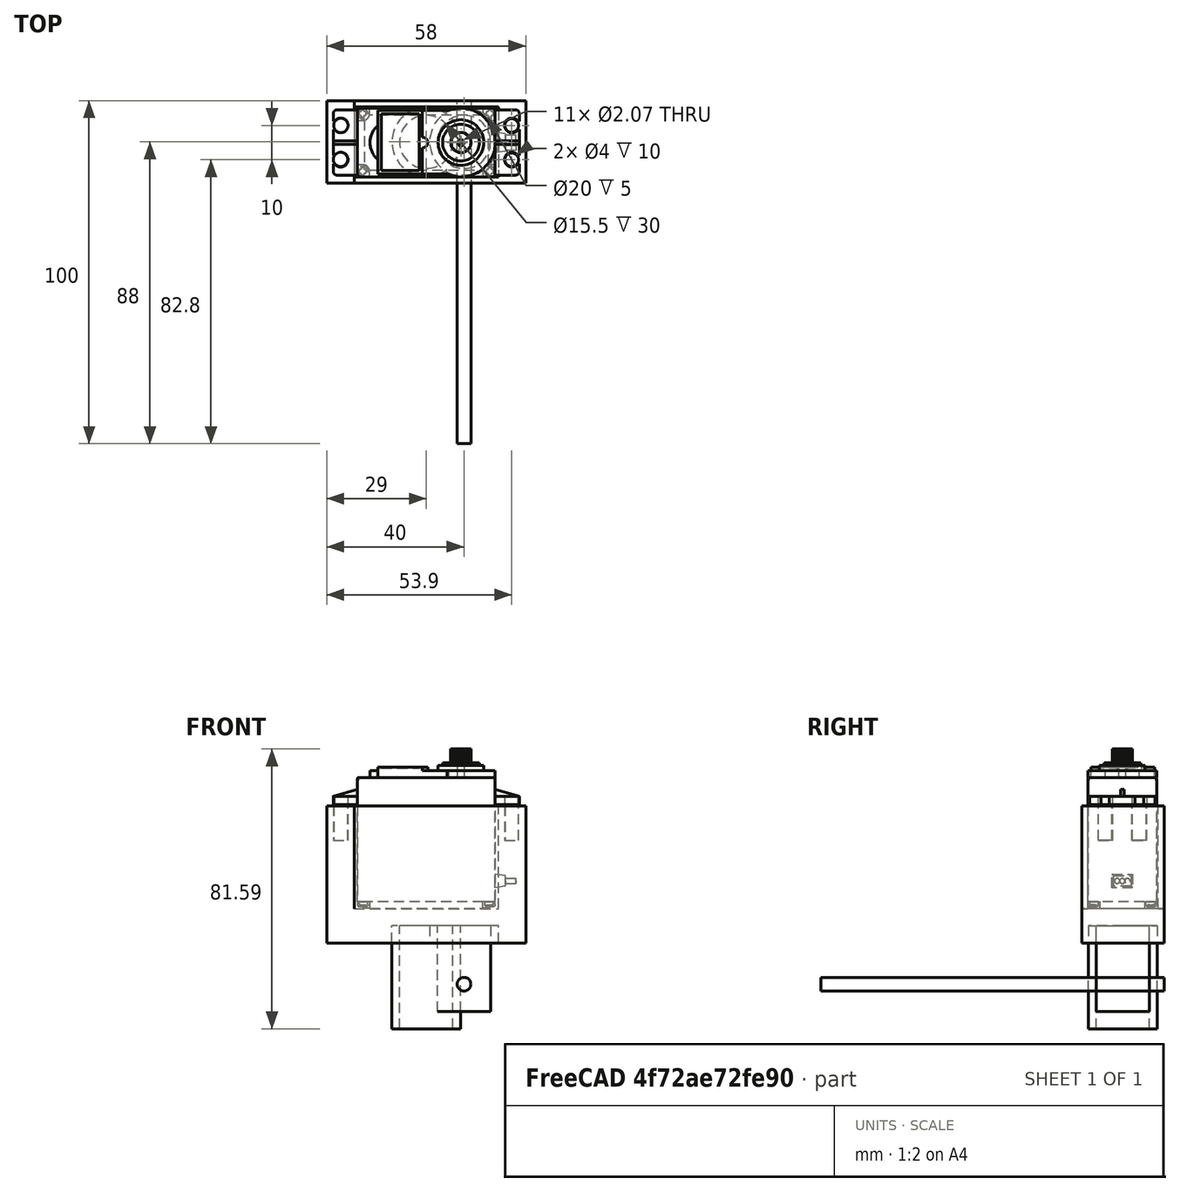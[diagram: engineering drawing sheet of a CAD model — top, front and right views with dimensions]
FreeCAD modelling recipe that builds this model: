
FCSTD DOCUMENT  (FreeCAD 0.21R33771 (Git))
Label: U_Servo_v1
License: All rights reserved
LicenseURL: http://en.wikipedia.org/wiki/All_rights_reserved
objects: Sketcher::SketchObject×5, PartDesign::Pad×3, Mesh::Feature×2, PartDesign::Pocket×2, Part::FeaturePython×1, Part::Feature×1, PartDesign::Body×1, Part::Cylinder×1
note: 19 computed .brp shape members not serialized (recipe doc carries the construction recipe); baked Part::Feature solids carry a one-line shape summary decoded from their .brp

FEATURE [Part::FeaturePython] Tube  # WARN: FeaturePython — macro-defined, semantics opaque (R4)
  AttacherType = Attacher::AttachEngine3D
  Height = 30
  InnerRadius = 7.75
  OuterRadius = 10
  Placement = pos=(0,-12,-37) rot=(0,0,1;0rad)
FEATURE [Mesh::Feature] servo_lower_cover_fake_shaft
FEATURE [Mesh::Feature] futaba  label="Servo"
  Placement = pos=(0,-3,2) rot=(0,0,1;0rad)
FEATURE [Part::Feature] Part__Feature  label="MG996R"
  Placement = pos=(0,-9,-0.5) rot=(0,0,1;0rad)
  shape: bbox 54.21 x 20.13 x 46.64 mm, 453 faces, 11 solids (baked)
FEATURE [Sketcher::SketchObject] Sketch
  FullyConstrained = false
  MapMode = 5
  Placement = pos=(0,0,0) rot=(1,0,0;1.5708rad)
  Support = -> [XZ_Plane]
  sketch-geometry (9):
    g0: LineSegment StartX=-21.001 StartY=28 StartZ=0 EndX=-29 EndY=28 EndZ=0
    g1: LineSegment StartX=-29 StartY=28 StartZ=0 EndX=-29 EndY=-2 EndZ=0
    g2: LineSegment StartX=21 StartY=28 StartZ=0 EndX=29 EndY=28 EndZ=0
    g3: LineSegment StartX=21 StartY=28 StartZ=0 EndX=21 EndY=-2 EndZ=0
    g4: LineSegment StartX=-21.001 StartY=28 StartZ=0 EndX=-21.001 EndY=-2 EndZ=0
    g5: LineSegment StartX=-29 StartY=-2 StartZ=0 EndX=-29 EndY=-12 EndZ=0
    g6: LineSegment StartX=-29 StartY=-12 StartZ=0 EndX=29 EndY=-12 EndZ=0
    g7: LineSegment StartX=29 StartY=28 StartZ=0 EndX=29 EndY=-12 EndZ=0
    g8: LineSegment StartX=-21.001 StartY=-2 StartZ=0 EndX=21 EndY=-2 EndZ=0
  constraints (18):
    c: Horizontal(g0)
    c: Coincident(g1,g0)
    c: Vertical(g1)
    c: Horizontal(g2)
    c: Coincident(g3,g2)
    c: Vertical(g3)
    c: Coincident(g4,g0)
    c: Vertical(g4)
    c: Coincident(g5,g1)
    c: Vertical(g5)
    c: Coincident(g6,g5)
    c: Horizontal(g6)
    c: Coincident(g7,g2)
    c: Coincident(g7,g6)
    c: Vertical(g7)
    c: Coincident(g8,g4)
    c: Coincident(g8,g3)
    c: Horizontal(g8)
FEATURE [PartDesign::Pad] Pad
  Direction = (0,-1,2e-16)
  Length = 24
  Length2 = 10
  Placement = pos=(0,0,0) rot=(1,0,0;1.5708rad)
  Profile = -> Sketch
  ReferenceAxis = -> Sketch [N_Axis]
  Type = 0
FEATURE [Sketcher::SketchObject] Sketch001
  FullyConstrained = false
  MapMode = 5
  Placement = pos=(0,-7.9e-15,-12) rot=(1,0,0;3.14159rad)
  Support = -> [Pad]
  sketch-geometry (1):
    g0: Circle CenterX=11 CenterY=12 CenterZ=0 NormalX=0 NormalY=0 NormalZ=1 AngleXU=0 Radius=10
FEATURE [Sketcher::SketchObject] Sketch003
  FullyConstrained = false
  MapMode = 5
  Placement = pos=(0,0,-2) rot=(0,0,1;3.14159rad)
  sketch-geometry (8):
    g0: LineSegment StartX=21 StartY=1.8 StartZ=0 EndX=21 EndY=0 EndZ=0
    g1: LineSegment StartX=-21 StartY=0 StartZ=0 EndX=-21 EndY=1.8 EndZ=0
    g2: LineSegment StartX=21 StartY=24 StartZ=0 EndX=21 EndY=22.2 EndZ=0
    g3: LineSegment StartX=-21 StartY=22.2 StartZ=0 EndX=-21 EndY=24 EndZ=0
    g4: LineSegment StartX=-21 StartY=24 StartZ=0 EndX=21 EndY=24 EndZ=0
    g5: LineSegment StartX=21 StartY=22.2 StartZ=0 EndX=-21 EndY=22.2 EndZ=0
    g6: LineSegment StartX=-21 StartY=1.8 StartZ=0 EndX=21 EndY=1.8 EndZ=0
    g7: LineSegment StartX=21 StartY=0 StartZ=0 EndX=-21 EndY=0 EndZ=0
  constraints (17):
    c: Vertical(g0)
    c: Vertical(g1)
    c: PointOnObject(g0,g-1)
    c: Vertical(g2)
    c: Vertical(g3)
    c: Coincident(g4,g3)
    c: Coincident(g4,g2)
    c: Horizontal(g4)
    c: Coincident(g5,g2)
    c: Coincident(g5,g3)
    c: Horizontal(g5)
    c: Coincident(g6,g1)
    c: Coincident(g6,g0)
    c: Horizontal(g6)
    c: Coincident(g7,g0)
    c: Coincident(g7,g1)
    c: Horizontal(g7)
FEATURE [PartDesign::Pad] Pad002
  BaseFeature = -> Pad
  Direction = (0,2e-16,1)
  Length = 30
  Length2 = 10
  Placement = pos=(0,0,0) rot=(1,0,0;1.5708rad)
  Profile = -> Sketch003
  ReferenceAxis = -> Sketch003 [N_Axis]
  Type = 0
FEATURE [PartDesign::Pocket] Pocket
  BaseFeature = -> Pad002
  Direction = (0,2e-16,1)
  Length = 5
  Length2 = 5
  Placement = pos=(0,0,0) rot=(1,0,0;1.5708rad)
  Profile = -> Sketch001
  ReferenceAxis = -> Sketch001 [N_Axis]
  Type = 0
FEATURE [Sketcher::SketchObject] Sketch004
  FullyConstrained = false
  MapMode = 5
  Placement = pos=(4e-16,-3.7e-15,-7) rot=(1,0,0;3.14159rad)
  Support = -> [Pocket]
  sketch-geometry (1):
    g0: Circle CenterX=11 CenterY=12 CenterZ=0 NormalX=0 NormalY=0 NormalZ=1 AngleXU=0 Radius=7.75
FEATURE [PartDesign::Pad] Pad003
  BaseFeature = -> Pocket
  Direction = (1e-16,-3e-16,-1)
  Length = 25
  Length2 = 10
  Placement = pos=(0,0,0) rot=(1,0,0;1.5708rad)
  Profile = -> Sketch004
  ReferenceAxis = -> Sketch004 [N_Axis]
  Type = 0
FEATURE [Sketcher::SketchObject] Sketch005
  FullyConstrained = false
  MapMode = 5
  Placement = pos=(0,1.85e-14,28) rot=(0,0,1;3.14159rad)
  Support = -> [Pad003]
  sketch-geometry (4):
    g0: Circle CenterX=-24.9 CenterY=17.2 CenterZ=0 NormalX=0 NormalY=0 NormalZ=1 AngleXU=0 Radius=2.00012
    g1: Circle CenterX=-24.9 CenterY=7.2 CenterZ=0 NormalX=0 NormalY=0 NormalZ=1 AngleXU=0 Radius=2.00121
    g2: Circle CenterX=24.9 CenterY=7.2 CenterZ=0 NormalX=0 NormalY=0 NormalZ=1 AngleXU=0 Radius=2.1
    g3: Circle CenterX=25 CenterY=17.1 CenterZ=0 NormalX=0 NormalY=0 NormalZ=1 AngleXU=0 Radius=2.10238
FEATURE [PartDesign::Pocket] Pocket001
  BaseFeature = -> Pad003
  Direction = (0,-2e-16,-1)
  Length = 10
  Length2 = 5
  Placement = pos=(0,0,0) rot=(1,0,0;1.5708rad)
  Profile = -> Sketch005
  ReferenceAxis = -> Sketch005 [N_Axis]
  Type = 0
FEATURE [PartDesign::Body] Body  label="U Servo Bracket"
  Group = -> [Sketch,Pad,Sketch001,Sketch003,Pad002,Pocket,Sketch004,Pad003,Sketch005,Pocket001]
  Origin = -> Origin
  Tip = -> Pocket001
FEATURE [Part::Cylinder] Cylinder  label="Cilindro"
  Angle = 360
  AttacherType = Attacher::AttachEngine3D
  FirstAngle = 0
  Height = 100
  Placement = pos=(11,0,-24) rot=(1,0,0;1.5708rad)
  Radius = 2
  SecondAngle = 0
